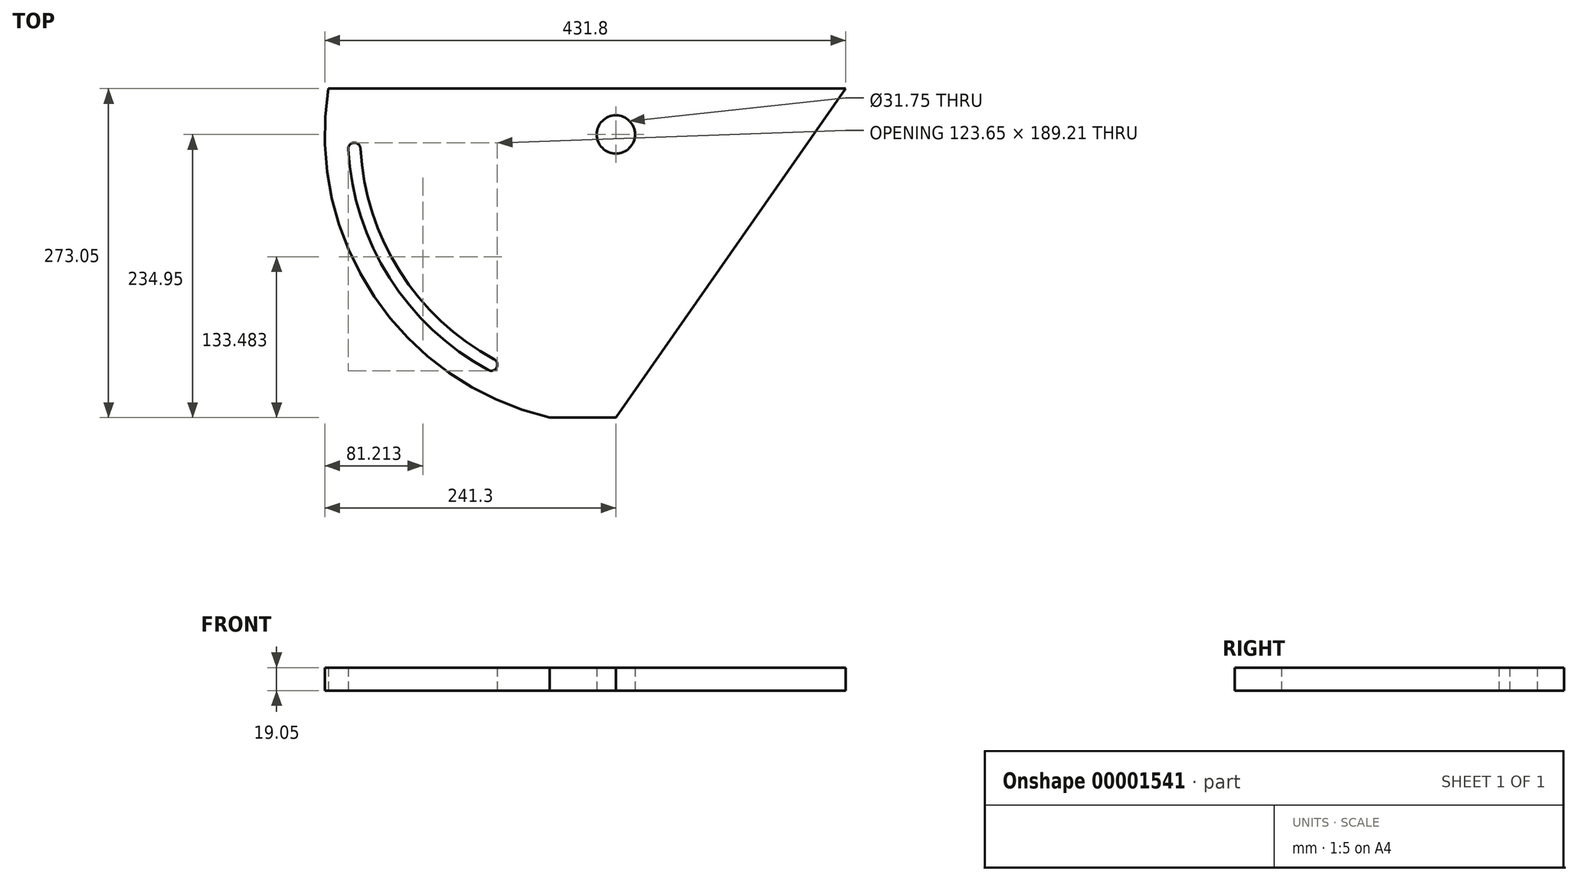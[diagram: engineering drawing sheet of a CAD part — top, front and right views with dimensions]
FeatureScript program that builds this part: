
annotation { "Feature Type Name" : "Feature", "Feature Type Description" : "" }
export const myFeature = defineFeature(function(context is Context, id is Id, definition is map)
    precondition{}
    {
        {
            var Q0;
            Q0=qCreatedBy(makeId("Top.planeOp"),FACE);
            var sketch = newSketch(context, id + "F0", { "sketchPlane" : qUnion([Q0])});
            skLineSegment(sketch, "E0", {"start": v(0, 0) * mm, "end": v(-428.77, 0) * mm});
            skLineSegment(sketch, "E1", {"start": v(-245.5, -273.05) * mm, "end": v(-190.5, -273.05) * mm});
            skLineSegment(sketch, "E2", {"start": v(-190.5, -273.05) * mm, "end": v(0, 0) * mm});
            skCircle(sketch, "E3", {"center": v(-190.5, -38.1) * mm, "radius": 15.88 * mm});
            skArc(sketch, "E4", {"start": v(-428.77, 0) * mm, "mid": v(-390.85, -172.58) * mm, "end": v(-245.5, -273.05) * mm});
            skArc(sketch, "E5", {"start": v(-412.41, -50.31) * mm, "mid": v(-378.21, -157.1) * mm, "end": v(-296.23, -233.59) * mm});
            skArc(sketch, "E6", {"start": v(-402.27, -49.75) * mm, "mid": v(-369.63, -151.65) * mm, "end": v(-291.4, -224.65) * mm});
            skArc(sketch, "E7", {"start": v(-402.27, -49.75) * mm, "mid": v(-407.62, -44.96) * mm, "end": v(-412.41, -50.31) * mm});
            skArc(sketch, "E8", {"start": v(-296.23, -233.59) * mm, "mid": v(-289.35, -231.54) * mm, "end": v(-291.4, -224.65) * mm});
            skSolve(sketch);
        }
        {
            var Q0;
            Q0=makeQuery(id+"F0.imprint","IMPRINT",FACE,{"disambiguationData":[TD([[makeQuery(id+"F0.imprint","IMPRINT",EDGE,{"derivedFrom":sQuery(id+"F0.wireOp",EDGE,"E0")}),1.0]])]});
            extrude(context, id + "F1", {"entities" : qUnion([Q0]), "depth" : 19.05 * mm});
        }
    });
